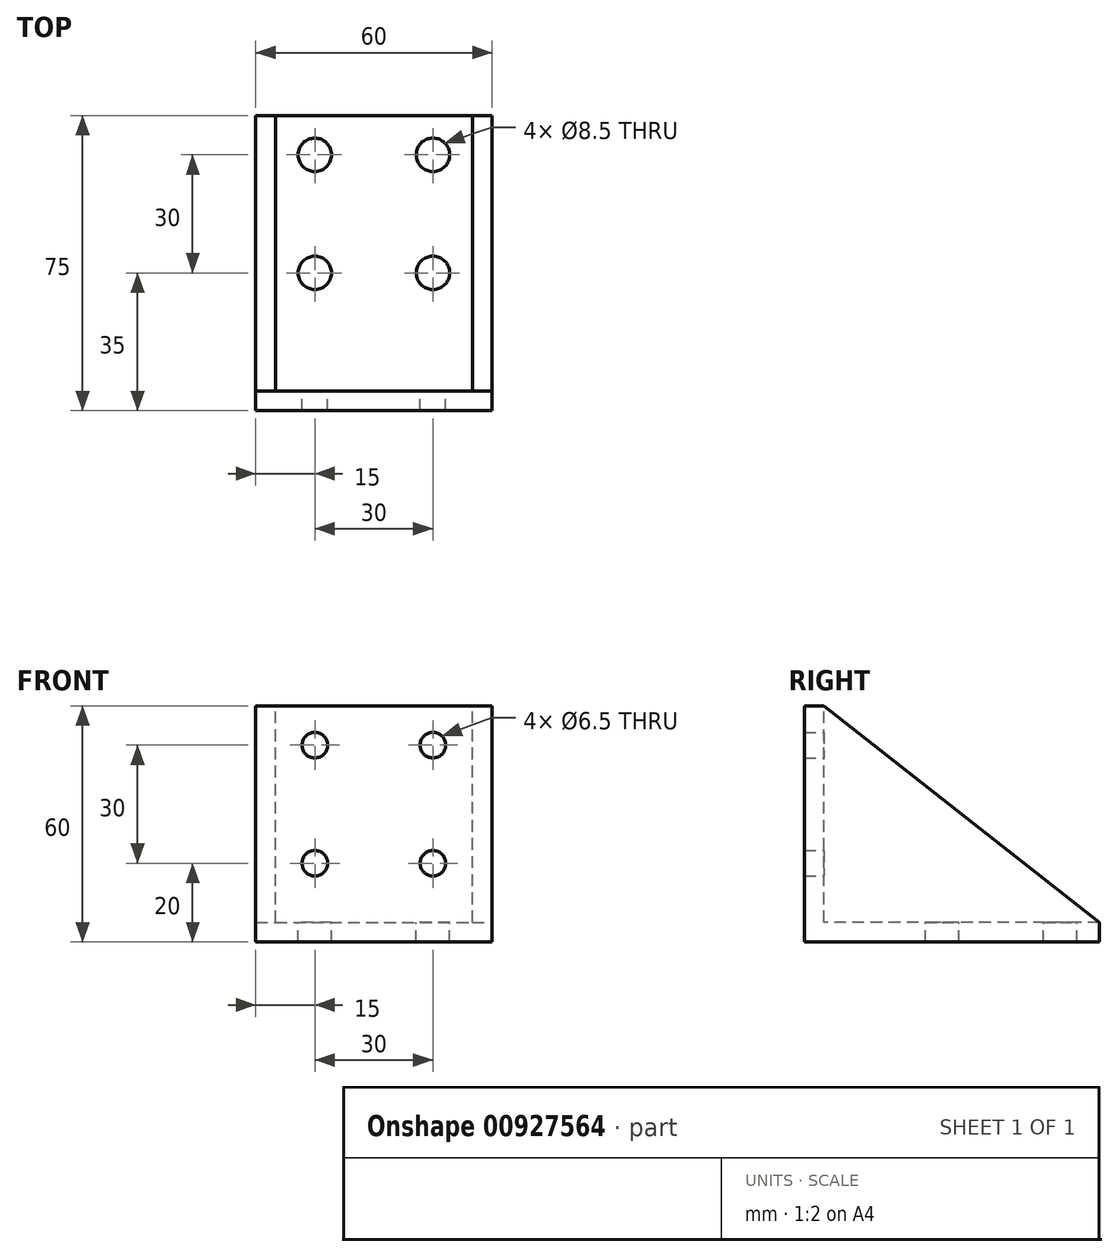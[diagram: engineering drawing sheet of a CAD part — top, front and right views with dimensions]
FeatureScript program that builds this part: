
annotation { "Feature Type Name" : "Feature", "Feature Type Description" : "" }
export const myFeature = defineFeature(function(context is Context, id is Id, definition is map)
    precondition{}
    {
        {
            var Q0;
            Q0=qCreatedBy(makeId("Right.planeOp"),FACE);
            var sketch = newSketch(context, id + "F0", { "sketchPlane" : qUnion([Q0])});
            skLineSegment(sketch, "E0", {"start": v(0, 0) * mm, "end": v(75, 0) * mm});
            skLineSegment(sketch, "E1", {"start": v(0, 0) * mm, "end": v(0, 60) * mm});
            skLineSegment(sketch, "E2.0", {"start": v(5, 5) * mm, "end": v(5, 60) * mm});
            skLineSegment(sketch, "E2.1", {"start": v(5, 5) * mm, "end": v(75, 5) * mm});
            skLineSegment(sketch, "E3", {"start": v(0, 60) * mm, "end": v(5, 60) * mm});
            skLineSegment(sketch, "E4", {"start": v(75, 5) * mm, "end": v(75, 0) * mm});
            skSolve(sketch);
        }
        {
            var Q0;
            Q0 = qSketchRegion(id + "F0", true);
            extrude(context, id + "F1", {"entities" : qUnion([Q0]), "oppositeDirection" : true, "depth" : 60 * mm, "offsetDistance" : 25 * mm});
        }
        {
            var Q0;
            Q0=qCreatedBy(makeId("Right.planeOp"),FACE);
            var sketch = newSketch(context, id + "F2", { "sketchPlane" : qUnion([Q0])});
            skLineSegment(sketch, "E5", {"start": v(5, 60) * mm, "end": v(75, 5) * mm});
            skLineSegment(sketch, "E6", {"start": v(75, 5) * mm, "end": v(5, 5) * mm});
            skLineSegment(sketch, "E7", {"start": v(5, 5) * mm, "end": v(5, 60) * mm});
            skSolve(sketch);
        }
        {
            var Q0;
            Q0 = qSketchRegion(id + "F2", true);
            extrude(context, id + "F3", {"entities" : qUnion([Q0]), "operationType" : NewBodyOperationType.ADD, "oppositeDirection" : true, "depth" : 5 * mm, "offsetDistance" : 25 * mm});
        }
        {
            var Q0;
            Q0=qCreatedBy(makeId("Right.planeOp"),FACE);
            cPlane(context, id + "F4", {"entities" : qUnion([Q0]), "cplaneType" : CPlaneType.OFFSET, "offset" : 60 * mm, "oppositeDirection" : true, "width" : 150 * mm, "height" : 150 * mm});
        }
        {
            var Q0;
            Q0=qCreatedBy(id+"F4.planeOp",FACE);
            var sketch = newSketch(context, id + "F5", { "sketchPlane" : qUnion([Q0])});
            skLineSegment(sketch, "E8", {"start": v(5, 60) * mm, "end": v(75, 5) * mm});
            skLineSegment(sketch, "E9", {"start": v(75, 5) * mm, "end": v(5, 5) * mm});
            skLineSegment(sketch, "E10", {"start": v(5, 5) * mm, "end": v(5, 60) * mm});
            skSolve(sketch);
        }
        {
            var Q0;
            Q0 = qSketchRegion(id + "F5", true);
            extrude(context, id + "F6", {"entities" : qUnion([Q0]), "operationType" : NewBodyOperationType.ADD, "depth" : 5 * mm, "offsetDistance" : 25 * mm});
        }
        {
            var Q0;
            Q0=makeQuery(id+"F1.opExtrude","SWEPT_FACE",FACE,{"disambiguationData":[OSD([sQuery(id+"F0.wireOp",EDGE,"E2.1")])]});
            var sketch = newSketch(context, id + "F7", { "sketchPlane" : qUnion([Q0])});
            skLineSegment(sketch, "E11", {"start": v(-30, 83.57) * mm, "end": v(-30, -23.18) * mm, "construction": true});
            skPoint(sketch, "E11.startSnap0", {"position": v(-30, 75) * mm});
            skCircle(sketch, "E12", {"center": v(-15, 35) * mm, "radius": 4.25 * mm});
            skCircle(sketch, "E13", {"center": v(-15, 65) * mm, "radius": 4.25 * mm});
            skCircle(sketch, "E14.MirrorC", {"center": v(-45, 65) * mm, "radius": 4.25 * mm});
            skCircle(sketch, "E15.MirrorC", {"center": v(-45, 35) * mm, "radius": 4.25 * mm});
            skSolve(sketch);
        }
        {
            var Q0;
            Q0 = qSketchRegion(id + "F7", true);
            extrude(context, id + "F8", {"entities" : qUnion([Q0]), "operationType" : NewBodyOperationType.REMOVE, "oppositeDirection" : true, "depth" : 25 * mm, "offsetDistance" : 25 * mm});
        }
        {
            var Q0;
            Q0=makeQuery(id+"F1.opExtrude","SWEPT_FACE",FACE,{"disambiguationData":[OSD([sQuery(id+"F0.wireOp",EDGE,"E2.0")])]});
            var sketch = newSketch(context, id + "F9", { "sketchPlane" : qUnion([Q0])});
            skLineSegment(sketch, "E16", {"start": v(30, 69.06) * mm, "end": v(30, -6.43) * mm, "construction": true});
            skPoint(sketch, "E16.startSnap0", {"position": v(30, 60) * mm});
            skCircle(sketch, "E17", {"center": v(45, 20) * mm, "radius": 3.25 * mm});
            skCircle(sketch, "E18", {"center": v(45, 50) * mm, "radius": 3.25 * mm});
            skCircle(sketch, "E19.MirrorC", {"center": v(15, 50) * mm, "radius": 3.25 * mm});
            skCircle(sketch, "E20.MirrorC", {"center": v(15, 20) * mm, "radius": 3.25 * mm});
            skSolve(sketch);
        }
        {
            var Q0;
            Q0 = qSketchRegion(id + "F9", true);
            extrude(context, id + "F10", {"entities" : qUnion([Q0]), "operationType" : NewBodyOperationType.REMOVE, "oppositeDirection" : true, "depth" : 25 * mm, "offsetDistance" : 25 * mm});
        }
    });
